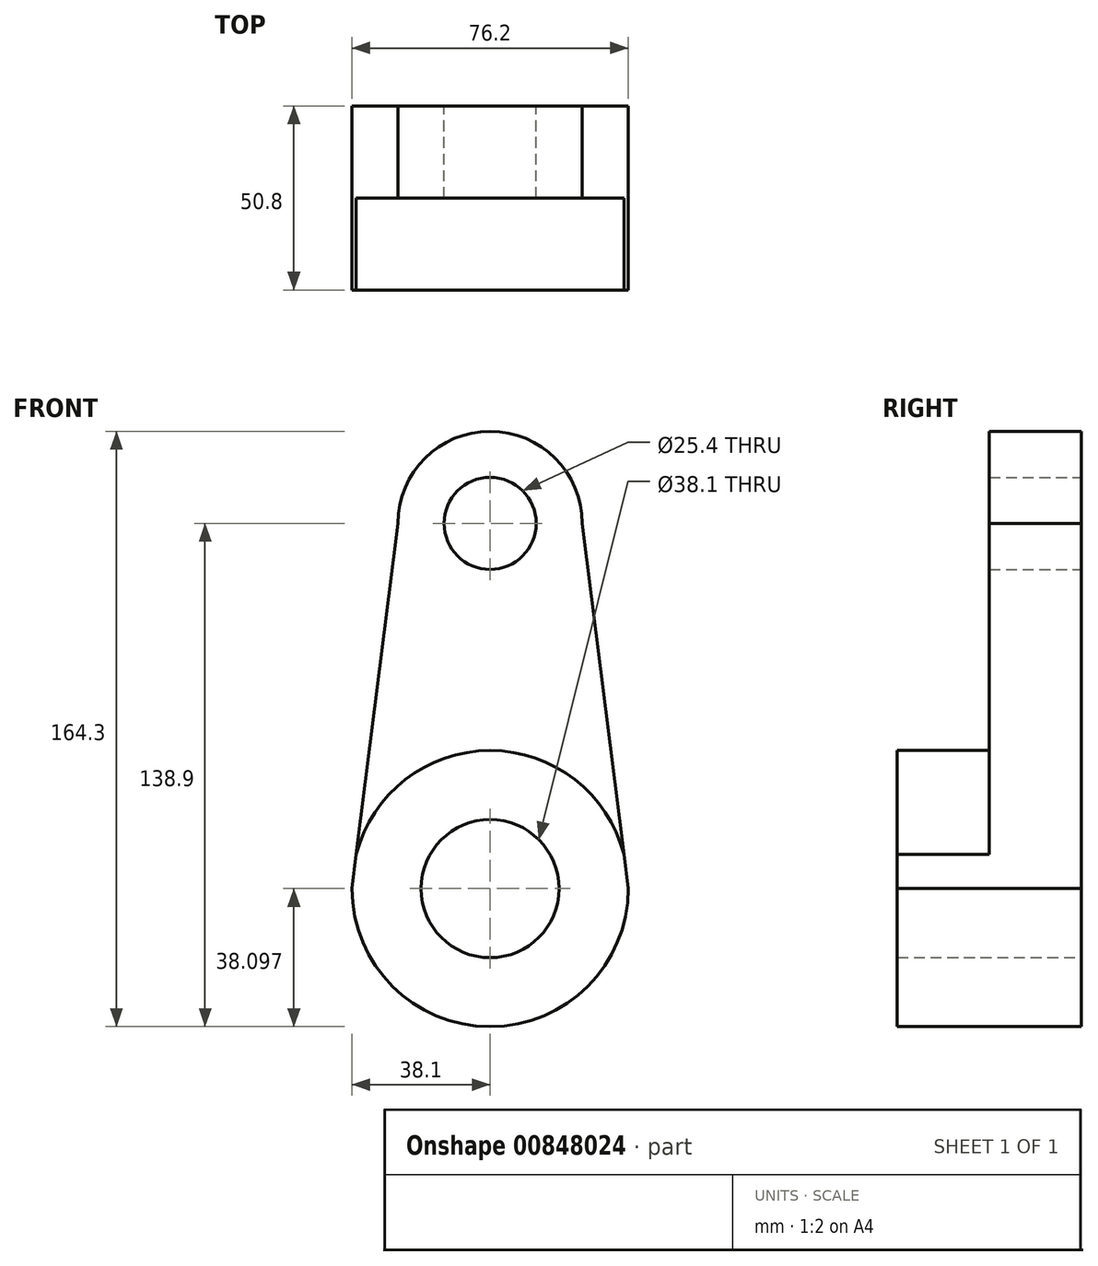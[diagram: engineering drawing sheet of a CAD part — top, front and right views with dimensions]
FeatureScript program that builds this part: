
annotation { "Feature Type Name" : "Feature", "Feature Type Description" : "" }
export const myFeature = defineFeature(function(context is Context, id is Id, definition is map)
    precondition{}
    {
        {
            var Q0;
            Q0=qCreatedBy(makeId("Front.planeOp"),FACE);
            var sketch = newSketch(context, id + "F0", { "sketchPlane" : qUnion([Q0])});
            skCircle(sketch, "E0", {"center": v(0, 0) * mm, "radius": 12.7 * mm});
            skCircle(sketch, "E1", {"center": v(0, 0) * mm, "radius": 25.4 * mm});
            skCircle(sketch, "E2", {"center": v(0, -100.8) * mm, "radius": 19.05 * mm});
            skCircle(sketch, "E3", {"center": v(0, -100.8) * mm, "radius": 38.1 * mm});
            skLineSegment(sketch, "E4", {"start": v(-25.4, 0) * mm, "end": v(-38.1, -100.8) * mm});
            skLineSegment(sketch, "E5", {"start": v(25.4, 0) * mm, "end": v(38.1, -100.8) * mm});
            skSolve(sketch);
        }
        {
            var Q0;
            Q0=makeQuery(id+"F0.imprint","IMPRINT",FACE,{"disambiguationData":[TD([[makeQuery(id+"F0.imprint","IMPRINT",EDGE,{"derivedFrom":sQuery(id+"F0.wireOp",EDGE,"E0")}),-1.0]])]});
            var Q1;
            {var subQ0=sQuery(id+"F0.wireOp",EDGE,"E4");var subQ1=sQuery(id+"F0.wireOp",EDGE,"E1");var subQ2=makeQuery(id+"F0.imprint","INTERSECT",VERTEX,{"derivedFrom":[subQ1,subQ0]});Q1=makeQuery(id+"F0.imprint","IMPRINT",FACE,{"disambiguationData":[TD([[makeQuery(id+"F0.imprint","IMPRINT",EDGE,{"disambiguationData":[TD([[subQ2,-1.0]])],"derivedFrom":subQ1}),-1.0]])]});}
            extrude(context, id + "F1", {"entities" : qUnion([Q0, Q1]), "depth" : 25.4 * mm, "offsetDistance" : 25.4 * mm});
        }
        {
            var Q0;
            Q0=makeQuery(id+"F0.imprint","IMPRINT",FACE,{"disambiguationData":[TD([[makeQuery(id+"F0.imprint","IMPRINT",EDGE,{"derivedFrom":sQuery(id+"F0.wireOp",EDGE,"E2")}),-1.0]])]});
            extrude(context, id + "F2", {"entities" : qUnion([Q0]), "operationType" : NewBodyOperationType.ADD, "depth" : 50.8 * mm, "offsetDistance" : 25.4 * mm});
        }
    });
